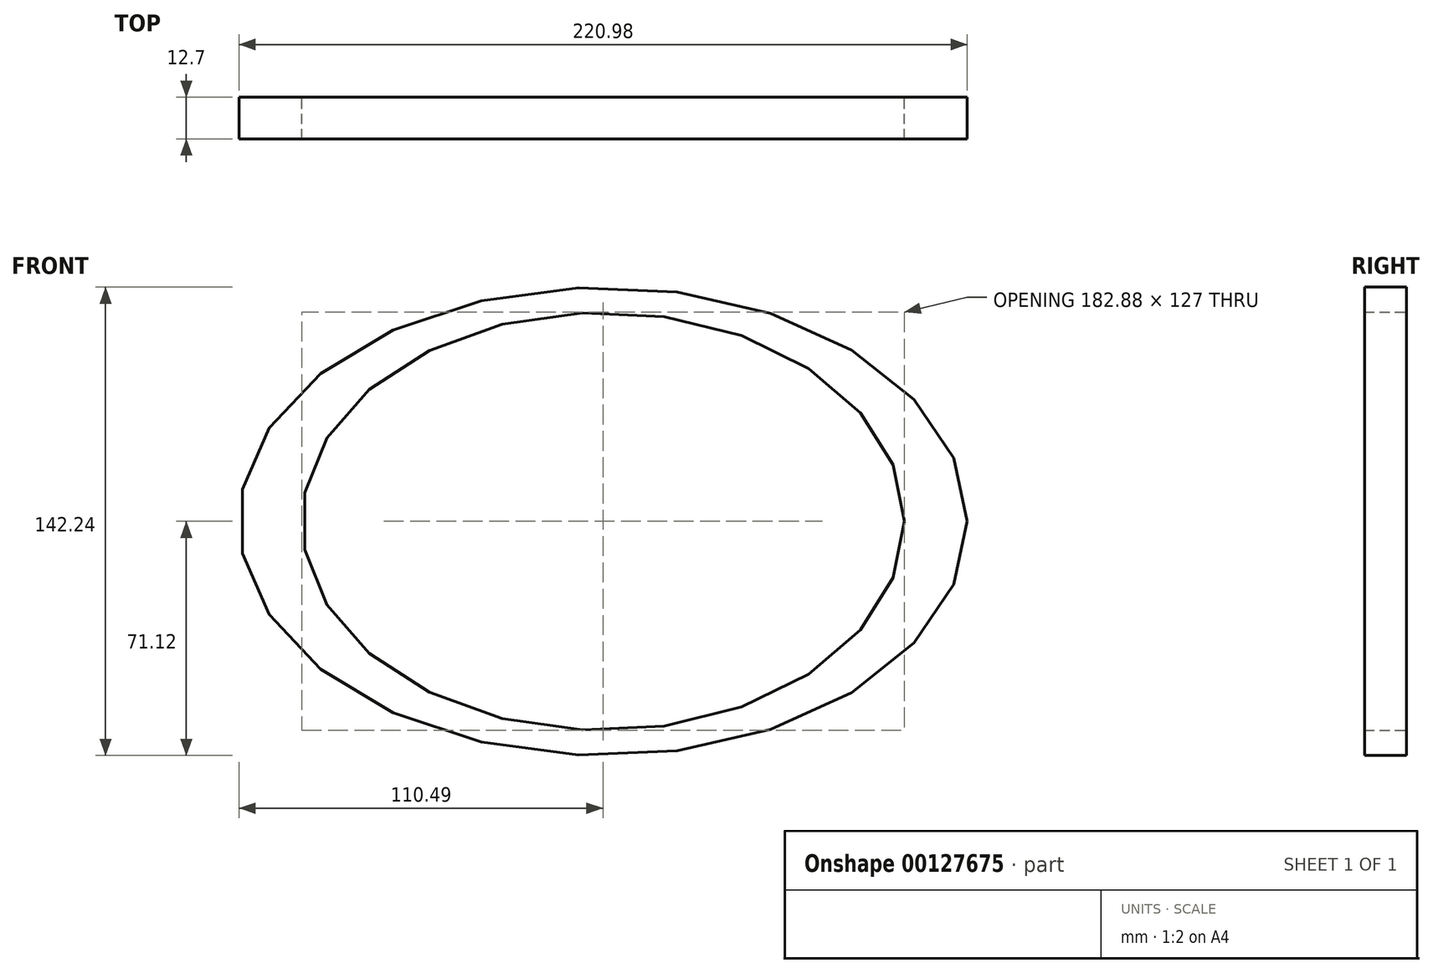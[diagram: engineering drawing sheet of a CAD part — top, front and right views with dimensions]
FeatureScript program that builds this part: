
annotation { "Feature Type Name" : "Feature", "Feature Type Description" : "" }
export const myFeature = defineFeature(function(context is Context, id is Id, definition is map)
    precondition{}
    {
        {
            var Q0;
            Q0=qCreatedBy(makeId("Front.planeOp"),FACE);
            var sketch = newSketch(context, id + "F0", { "sketchPlane" : qUnion([Q0])});
            skEllipse(sketch, "E0", {"center": v(0, 0) * mm, "majorRadius": 91.44 * mm, "minorRadius": 63.5 * mm, "majorAxis": v(1, 0)});
            skEllipse(sketch, "E1", {"center": v(0, 0) * mm, "majorRadius": 110.5 * mm, "minorRadius": 71.12 * mm, "majorAxis": v(1, 0)});
            skSolve(sketch);
        }
        {
            var Q0;
            Q0=makeQuery(id+"F0.imprint","IMPRINT",FACE,{"disambiguationData":[TD([[makeQuery(id+"F0.imprint","IMPRINT",EDGE,{"derivedFrom":sQuery(id+"F0.wireOp",EDGE,"E0")}),-1.0]])]});
            extrude(context, id + "F1", {"entities" : qUnion([Q0]), "depth" : 12.7 * mm});
        }
    });
